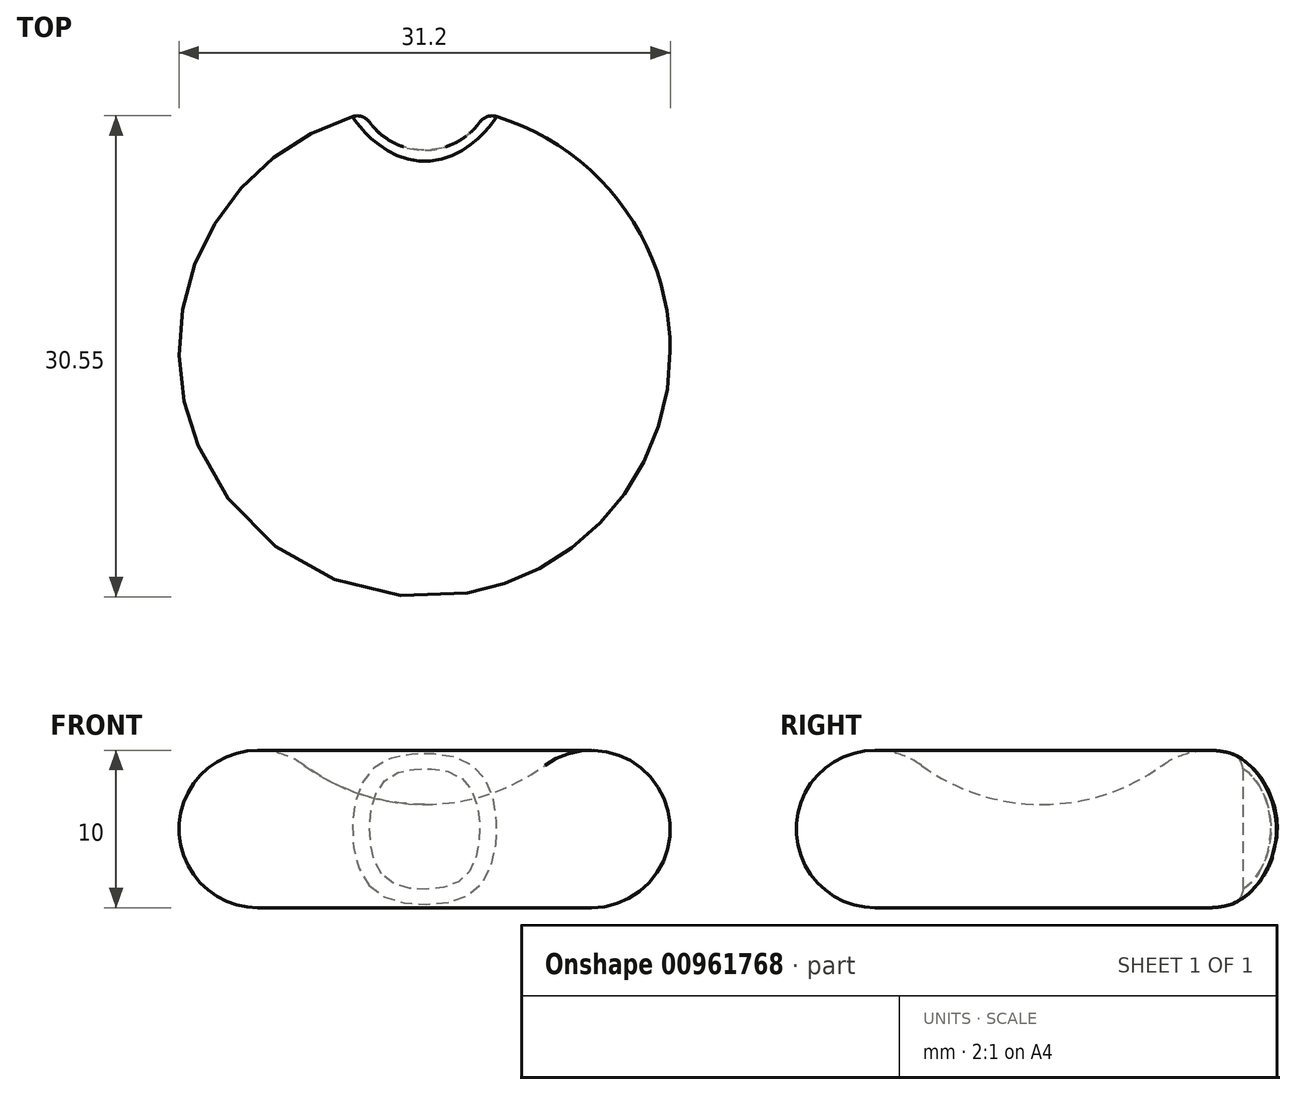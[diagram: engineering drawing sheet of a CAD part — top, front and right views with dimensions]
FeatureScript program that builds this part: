
annotation { "Feature Type Name" : "Feature", "Feature Type Description" : "" }
export const myFeature = defineFeature(function(context is Context, id is Id, definition is map)
    precondition{}
    {
        {
            var Q0;
            Q0=qCreatedBy(makeId("Front.planeOp"),FACE);
            var sketch = newSketch(context, id + "F0", { "sketchPlane" : qUnion([Q0])});
            skArc(sketch, "E0", {"start": v(-7.66, 9.05) * mm, "mid": v(-15.35, 6.54) * mm, "end": v(-10.6, 0) * mm});
            skArc(sketch, "E1", {"start": v(-7.66, 9.05) * mm, "mid": v(-4.03, 7.2) * mm, "end": v(0, 6.56) * mm});
            skLineSegment(sketch, "E2", {"start": v(0, 0) * mm, "end": v(0, 6.56) * mm});
            skLineSegment(sketch, "E3", {"start": v(0, 6.56) * mm, "end": v(0, 0) * mm});
            skLineSegment(sketch, "E4", {"start": v(-10.68, 0) * mm, "end": v(0, 0) * mm});
            skSolve(sketch);
        }
        {
            var Q0;
            {var subQ0=sQuery(id+"F0.wireOp",EDGE,"E0");Q0=makeQuery(id+"F0.imprint","IMPRINT",FACE,{"disambiguationData":[TD([[makeQuery(id+"F0.imprint","IMPRINT",EDGE,{"derivedFrom":subQ0}),1.0]])]});}
            var Q1;
            Q1=sQuery(id+"F0.wireOp",EDGE,"E3");
            revolve(context, id + "F1", {"surfaceOperationType" : NewSurfaceOperationType.NEW, "entities" : qUnion([Q0]), "axis" : qUnion([Q1]), "revolveType" : RevolveType.FULL});
        }
        {
            var Q0;
            Q0=qCreatedBy(makeId("Top.planeOp"),FACE);
            var sketch = newSketch(context, id + "F2", { "sketchPlane" : qUnion([Q0])});
            skCircle(sketch, "E5", {"center": v(0, 17.09) * mm, "radius": 4.32 * mm});
            skSolve(sketch);
        }
        {
            var Q0;
            Q0 = qSketchRegion(id + "F2", true);
            extrude(context, id + "F3", {"entities" : qUnion([Q0]), "operationType" : NewBodyOperationType.REMOVE, "depth" : 25 * mm, "offsetDistance" : 25 * mm});
        }
        {
            var Q0;
            Q0=makeQuery(id+"F3.boolean.opBoolean","INTERSECT",EDGE,{"derivedFrom":[makeQuery(id+"F1.opRevolve","SWEPT_FACE",FACE,{"disambiguationData":[OSD([sQuery(id+"F0.wireOp",EDGE,"E0")])]}),makeQuery(id+"F3.opExtrude","SWEPT_FACE",FACE,{"disambiguationData":[OSD([sQuery(id+"F2.wireOp",EDGE,"E5")])]})]});
            fillet(context, id + "F4", {"entities" : qUnion([Q0]), "radius" : 1 * mm, "tangentPropagation" : true, "allowEdgeOverflow" : false});
        }
    });
